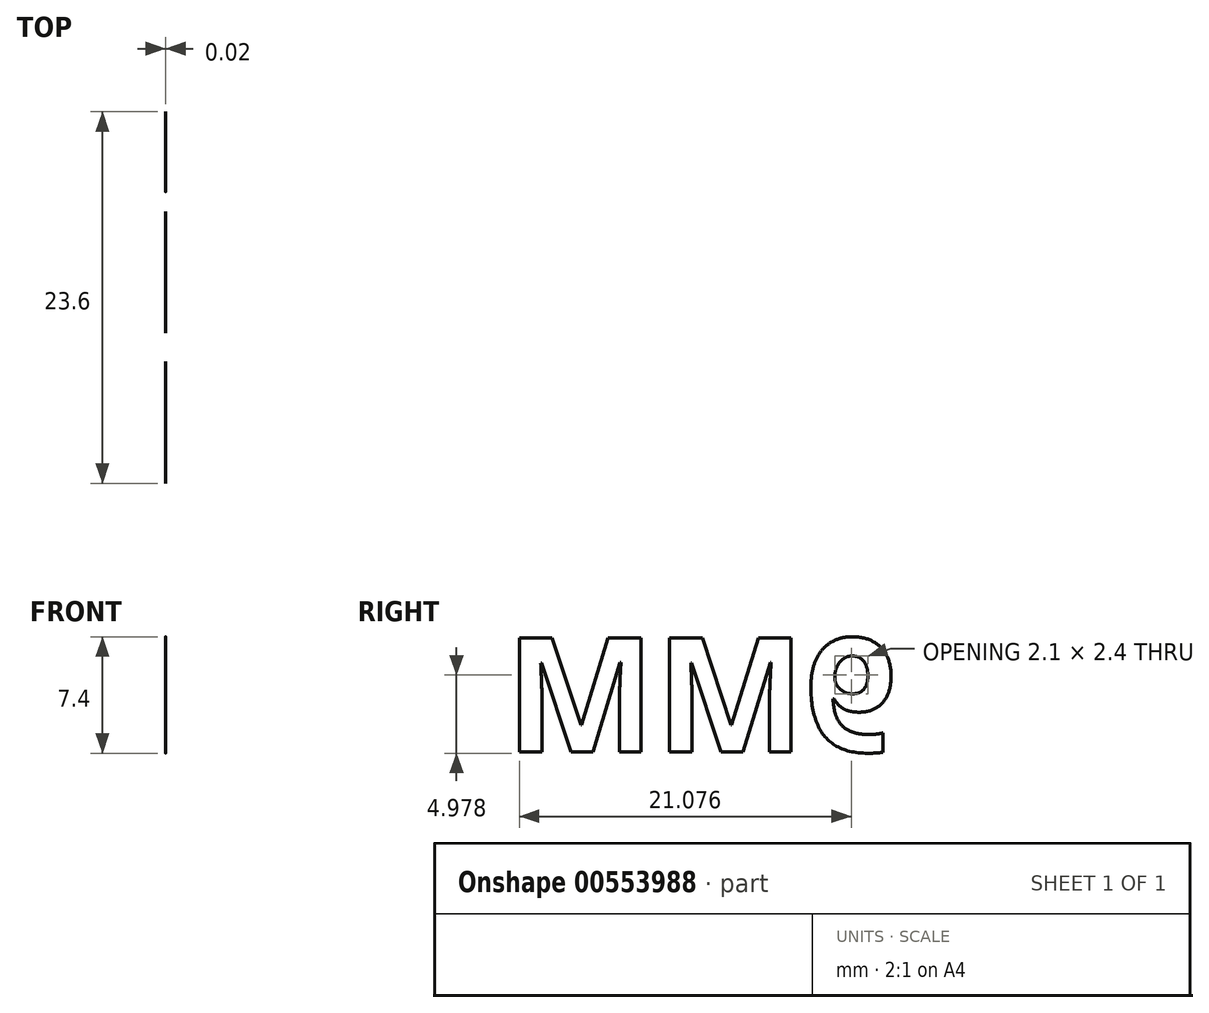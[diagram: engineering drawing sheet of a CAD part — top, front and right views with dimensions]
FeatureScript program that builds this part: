
annotation { "Feature Type Name" : "Feature", "Feature Type Description" : "" }
export const myFeature = defineFeature(function(context is Context, id is Id, definition is map)
    precondition{}
    {
        {
            var Q0;
            Q0=qCreatedBy(makeId("Front.planeOp"),FACE);
            var sketch = newSketch(context, id + "F0", { "sketchPlane" : qUnion([Q0])});
            skLineSegment(sketch, "E0", {"start": v(-75.45, 0) * mm, "end": v(123.38, 0) * mm, "construction": true});
            skArc(sketch, "E1", {"start": v(102.66, 0) * mm, "mid": v(57.19, 24.61) * mm, "end": v(6.36, 34.1) * mm});
            skLineSegment(sketch, "E2.bottom", {"start": v(6.36, 34.1) * mm, "end": v(-61.53, 34.1) * mm});
            skLineSegment(sketch, "E2.top", {"start": v(6.36, 0) * mm, "end": v(-61.53, 0) * mm});
            skLineSegment(sketch, "E2.right", {"start": v(-61.53, 34.1) * mm, "end": v(-61.53, 33.2) * mm});
            skLineSegment(sketch, "E3.bottom", {"start": v(-61.53, 33.2) * mm, "end": v(-63.48, 33.2) * mm});
            skLineSegment(sketch, "E3.top", {"start": v(-61.53, 0) * mm, "end": v(-63.48, 0) * mm});
            skLineSegment(sketch, "E4.bottom", {"start": v(-63.48, 34.1) * mm, "end": v(-71.93, 34.1) * mm});
            skLineSegment(sketch, "E4.top", {"start": v(-63.48, 0) * mm, "end": v(-71.93, 0) * mm});
            skLineSegment(sketch, "E4.left", {"start": v(-63.48, 34.1) * mm, "end": v(-63.48, 33.2) * mm});
            skLineSegment(sketch, "E4.right", {"start": v(-71.93, 34.1) * mm, "end": v(-71.93, 0) * mm});
            skSolve(sketch);
        }
        {
            var Q0;
            Q0=sQuery(id+"F0.wireOp",EDGE,"E1");
            var Q1;
            Q1=sQuery(id+"F0.wireOp",EDGE,"E3.bottom");
            var Q2;
            Q2=sQuery(id+"F0.wireOp",EDGE,"E4.bottom");
            var Q3;
            Q3=sQuery(id+"F0.wireOp",EDGE,"E2.bottom");
            var Q4;
            Q4=sQuery(id+"F0.wireOp",EDGE,"E2.right");
            var Q5;
            Q5=sQuery(id+"F0.wireOp",EDGE,"E4.right");
            var Q6;
            Q6=sQuery(id+"F0.wireOp",EDGE,"E0");
            revolve(context, id + "F1", {"bodyType" : ToolBodyType.SURFACE, "surfaceOperationType" : NewSurfaceOperationType.NEW, "surfaceEntities" : qUnion([Q0, Q1, Q2, Q3, Q4, Q5]), "axis" : qUnion([Q6]), "revolveType" : RevolveType.FULL});
        }
        {
            var Q0;
            Q0=makeQuery(id+"F1.opRevolve","SWEPT_FACE",FACE,{"disambiguationData":[OSD([sQuery(id+"F0.wireOp",EDGE,"E4.right")])]});
            var sketch = newSketch(context, id + "F2", { "sketchPlane" : qUnion([Q0])});
            skText(sketch, "E5", { "text": "9MM\n", "fontName": "OpenSans-Bold.ttf"});
            const initialGuessF2  = {"E5": [-0.01121, 0.02138, 1, 0, 0.00728]};
            skSetInitialGuess(sketch, initialGuessF2);
            skSolve(sketch);
        }
        {
            var Q0;
            Q0 = qSketchRegion(id + "F2", true);
            extrude(context, id + "F3", {"entities" : qUnion([Q0]), "depth" : 0.02 * mm, "offsetDistance" : 25 * mm});
        }
    });
